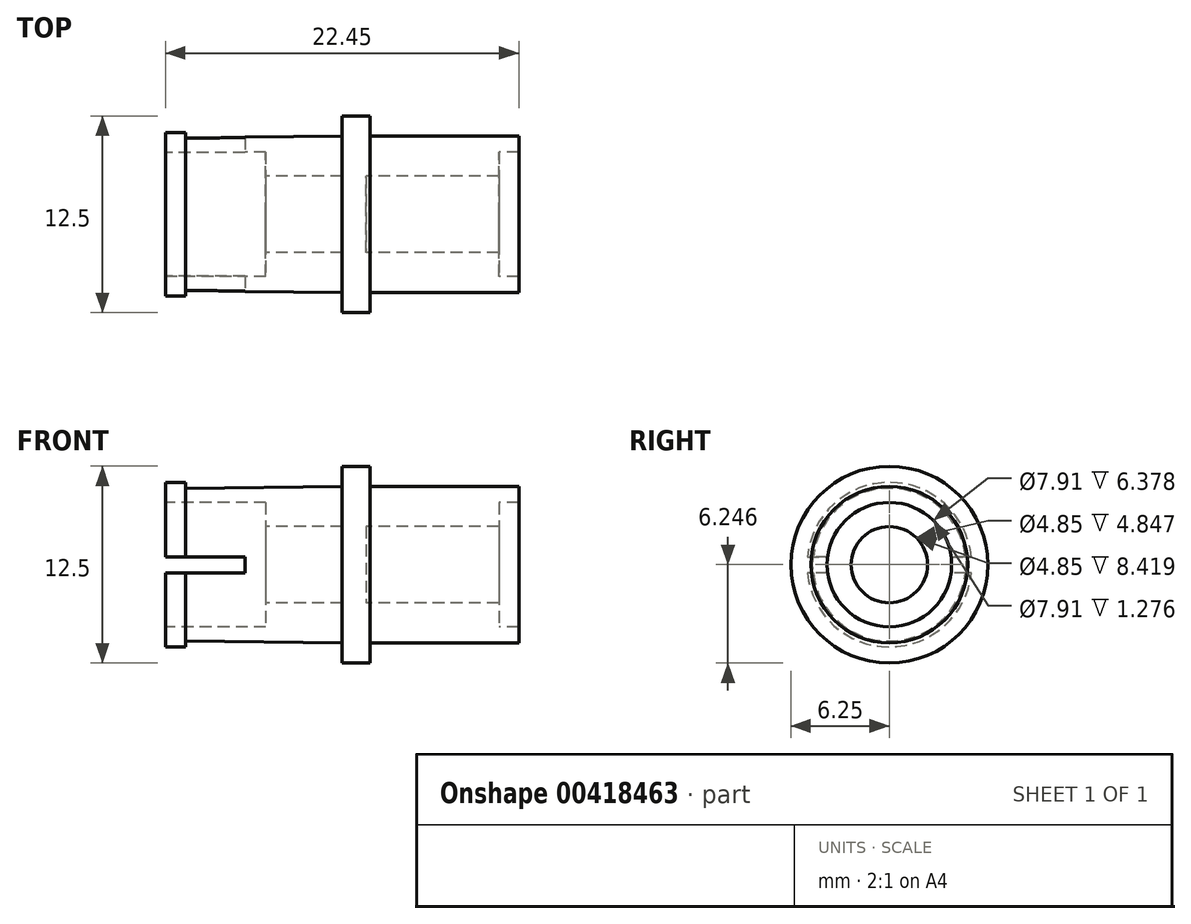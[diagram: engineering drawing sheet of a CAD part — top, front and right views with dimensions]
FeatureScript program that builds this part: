
annotation { "Feature Type Name" : "Feature", "Feature Type Description" : "" }
export const myFeature = defineFeature(function(context is Context, id is Id, definition is map)
    precondition{}
    {
        {
            var Q0;
            Q0=qCreatedBy(makeId("Front.planeOp"),FACE);
            var sketch = newSketch(context, id + "F0", { "sketchPlane" : qUnion([Q0])});
            skLineSegment(sketch, "E0", {"start": v(-13.01, 1.27) * mm, "end": v(-13.01, 0) * mm});
            skLineSegment(sketch, "E1", {"start": v(9.44, 1.02) * mm, "end": v(9.44, 0) * mm});
            skLineSegment(sketch, "E2", {"start": v(-13.01, 1.27) * mm, "end": v(-11.74, 1.27) * mm});
            skLineSegment(sketch, "E3", {"start": v(-13.01, 0) * mm, "end": v(-6.63, 0) * mm});
            skLineSegment(sketch, "E4", {"start": v(-6.63, 0) * mm, "end": v(-6.63, -1.53) * mm});
            skLineSegment(sketch, "E5", {"start": v(-6.63, -1.53) * mm, "end": v(-1.79, -1.53) * mm});
            skLineSegment(sketch, "E6", {"start": v(-1.79, -1.53) * mm, "end": v(-1.79, -3.95) * mm});
            skLineSegment(sketch, "E7", {"start": v(-1.79, -3.95) * mm, "end": v(-0.26, -3.95) * mm});
            skLineSegment(sketch, "E8", {"start": v(-0.26, -3.95) * mm, "end": v(-0.26, -1.53) * mm});
            skLineSegment(sketch, "E9", {"start": v(-0.26, -1.53) * mm, "end": v(8.16, -1.53) * mm});
            skLineSegment(sketch, "E10", {"start": v(8.16, -1.53) * mm, "end": v(8.16, 0) * mm});
            skLineSegment(sketch, "E11", {"start": v(9.44, 1.02) * mm, "end": v(0, 1.02) * mm});
            skLineSegment(sketch, "E12", {"start": v(0, 1.02) * mm, "end": v(0, 2.3) * mm});
            skLineSegment(sketch, "E13", {"start": v(0, 2.3) * mm, "end": v(-1.79, 2.3) * mm});
            skLineSegment(sketch, "E14", {"start": v(-1.79, 2.3) * mm, "end": v(-1.79, 1.02) * mm});
            skLineSegment(sketch, "E15", {"start": v(8.16, 0) * mm, "end": v(9.44, 0) * mm});
            skLineSegment(sketch, "E16", {"start": v(-11.74, 1.27) * mm, "end": v(-11.74, 0.9) * mm});
            skLineSegment(sketch, "E17", {"start": v(-11.74, 0.9) * mm, "end": v(-1.79, 1.02) * mm});
            skSolve(sketch);
        }
        {
            var Q0;
            Q0 = qSketchRegion(id + "F0", true);
            var Q1;
            Q1=sQuery(id+"F0.wireOp",EDGE,"E7");
            revolve(context, id + "F1", {"entities" : qUnion([Q0]), "axis" : qUnion([Q1]), "revolveType" : RevolveType.FULL});
        }
        {
            var Q0;
            Q0=qCreatedBy(makeId("Front.planeOp"),FACE);
            cPlane(context, id + "F2", {"entities" : qUnion([Q0]), "cplaneType" : CPlaneType.OFFSET, "offset" : 6.35 * mm, "width" : 152.4 * mm, "height" : 152.4 * mm});
        }
        {
            var Q0;
            Q0=qCreatedBy(id+"F2.planeOp",FACE);
            var sketch = newSketch(context, id + "F3", { "sketchPlane" : qUnion([Q0])});
            skPoint(sketch, "E18.endSnap0", {"position": v(-13.04, -3.47) * mm});
            skLineSegment(sketch, "E19", {"start": v(-13.04, -3.98) * mm, "end": v(-13.04, -4.49) * mm});
            skLineSegment(sketch, "E20", {"start": v(-13.04, -3.47) * mm, "end": v(-7.97, -3.47) * mm});
            skLineSegment(sketch, "E21", {"start": v(-7.97, -3.47) * mm, "end": v(-7.97, -4.48) * mm});
            skLineSegment(sketch, "E22", {"start": v(-7.97, -4.48) * mm, "end": v(-13.04, -4.49) * mm});
            skLineSegment(sketch, "E23", {"start": v(-13.04, -3.98) * mm, "end": v(-13.04, -3.47) * mm});
            skSolve(sketch);
        }
        {
            var Q0;
            Q0 = qSketchRegion(id + "F3", true);
            extrude(context, id + "F4", {"entities" : qUnion([Q0]), "operationType" : NewBodyOperationType.REMOVE, "oppositeDirection" : true, "depth" : 25.4 * mm});
        }
    });
